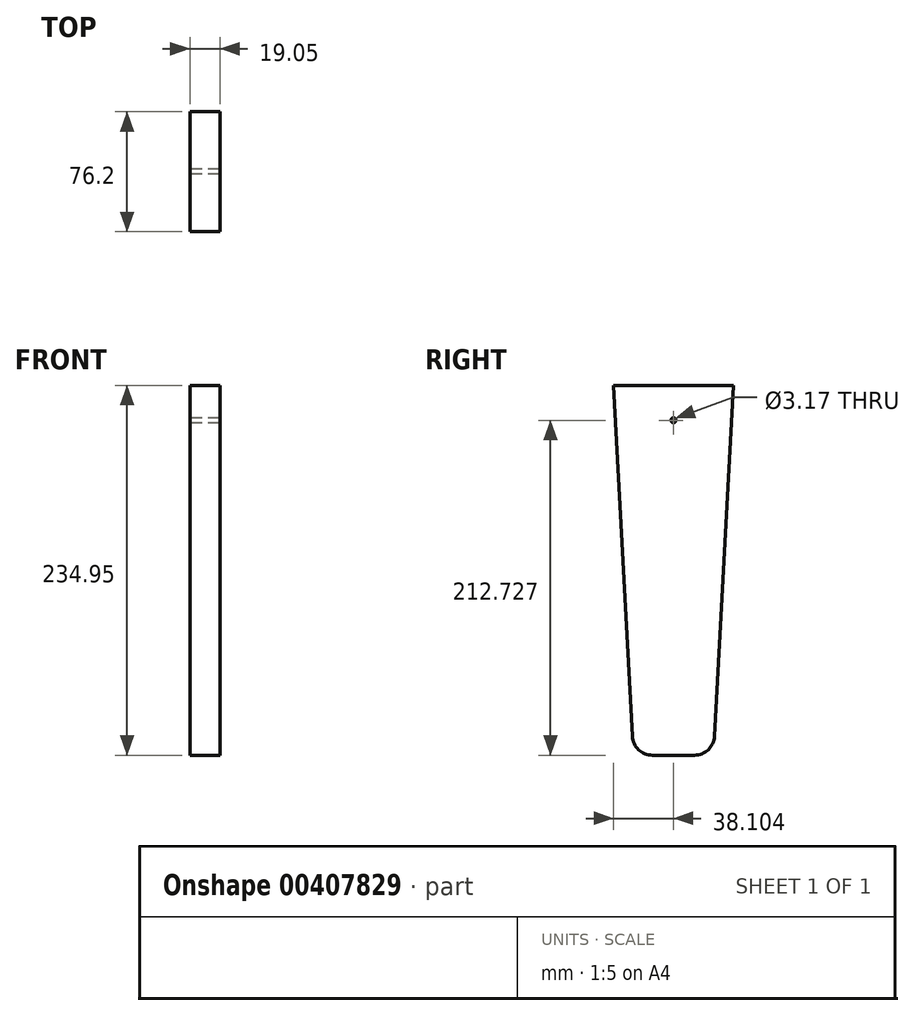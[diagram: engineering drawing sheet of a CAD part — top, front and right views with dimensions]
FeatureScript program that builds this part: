
annotation { "Feature Type Name" : "Feature", "Feature Type Description" : "" }
export const myFeature = defineFeature(function(context is Context, id is Id, definition is map)
    precondition{}
    {
        {
            var Q0;
            Q0=qCreatedBy(makeId("Right.planeOp"),FACE);
            var sketch = newSketch(context, id + "F0", { "sketchPlane" : qUnion([Q0])});
            skLineSegment(sketch, "E0", {"start": v(-29.4, -114.5) * mm, "end": v(-2.67, -114.5) * mm});
            skLineSegment(sketch, "E1", {"start": v(10.01, -102.5) * mm, "end": v(22.06, 120.44) * mm});
            skLineSegment(sketch, "E2", {"start": v(22.06, 120.44) * mm, "end": v(-54.14, 120.44) * mm});
            skLineSegment(sketch, "E3", {"start": v(-54.14, 120.44) * mm, "end": v(-42.09, -102.5) * mm});
            skCircle(sketch, "E4", {"center": v(-16.04, 98.22) * mm, "radius": 1.59 * mm});
            skPoint(sketch, "E5.visualSharp", {"position": v(9.36, -114.5) * mm});
            skArc(sketch, "E5.filletArc", {"start": v(-2.67, -114.5) * mm, "mid": v(6.07, -111.03) * mm, "end": v(10.01, -102.5) * mm});
            skPoint(sketch, "E6.visualSharp", {"position": v(-41.44, -114.5) * mm});
            skArc(sketch, "E6.filletArc", {"start": v(-42.09, -102.5) * mm, "mid": v(-38.14, -111.03) * mm, "end": v(-29.4, -114.5) * mm});
            skSolve(sketch);
        }
        {
            var Q0;
            Q0=makeQuery(id+"F0.imprint","IMPRINT",FACE,{"disambiguationData":[TD([[makeQuery(id+"F0.imprint","IMPRINT",EDGE,{"derivedFrom":sQuery(id+"F0.wireOp",EDGE,"E0")}),1.0]])]});
            extrude(context, id + "F1", {"entities" : qUnion([Q0]), "depth" : 19.05 * mm});
        }
    });
